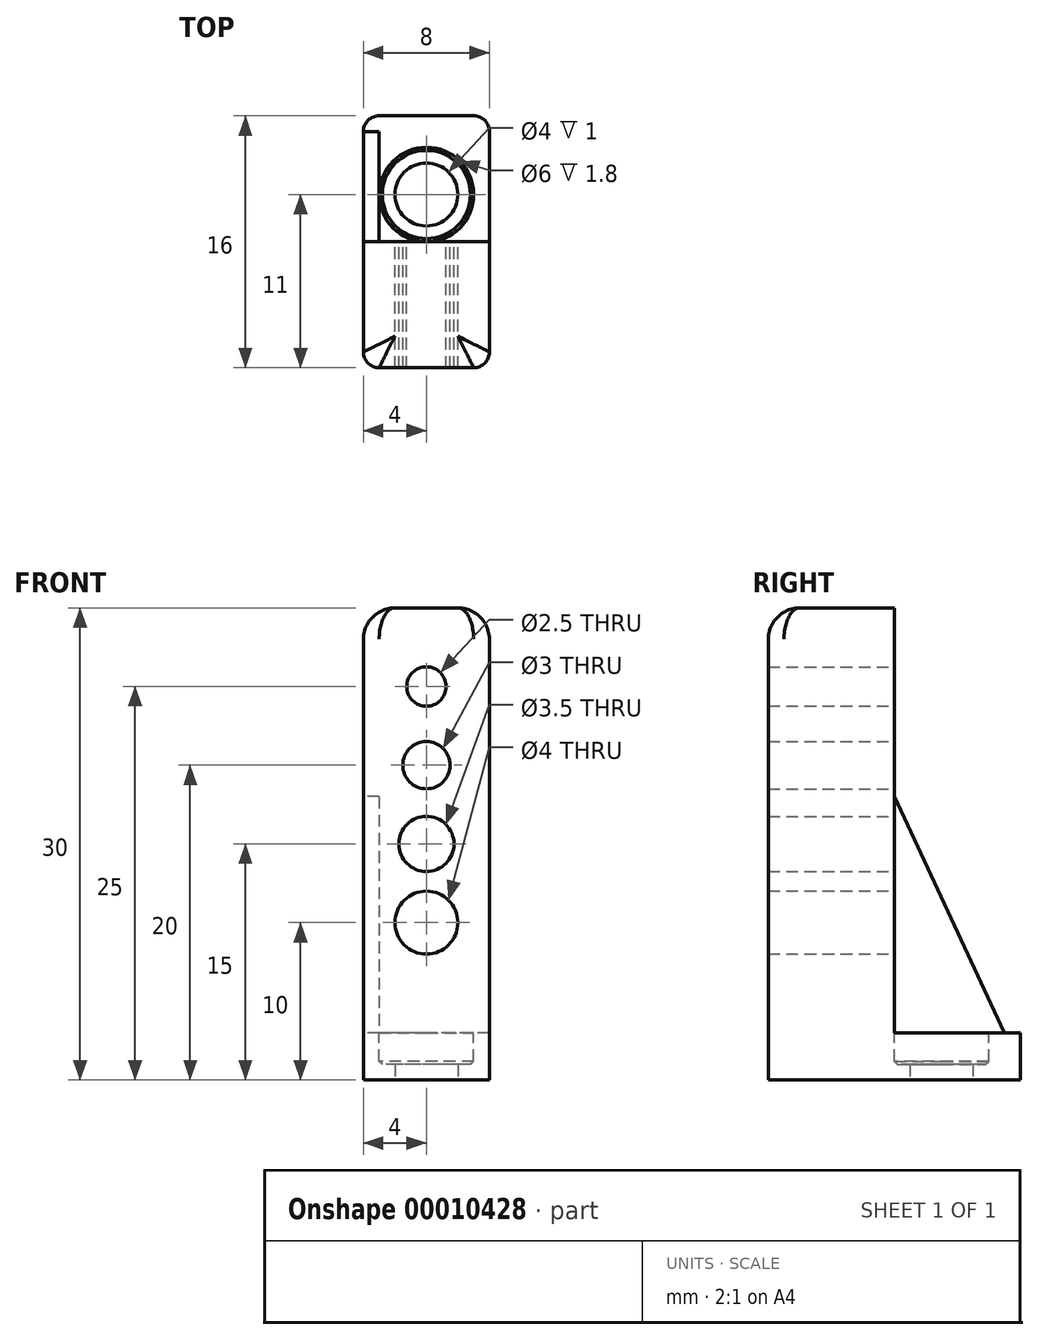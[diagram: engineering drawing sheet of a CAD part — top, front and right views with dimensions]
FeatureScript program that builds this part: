
annotation { "Feature Type Name" : "Feature", "Feature Type Description" : "" }
export const myFeature = defineFeature(function(context is Context, id is Id, definition is map)
    precondition{}
    {
        {
            var Q0;
            Q0=qCreatedBy(makeId("Top.planeOp"),FACE);
            var sketch = newSketch(context, id + "F0", { "sketchPlane" : qUnion([Q0])});
            skLineSegment(sketch, "E0.bottom", {"start": v(3, 5) * mm, "end": v(-3, 5) * mm});
            skLineSegment(sketch, "E0.top", {"start": v(4, -5) * mm, "end": v(-4, -5) * mm});
            skLineSegment(sketch, "E0.left", {"start": v(4, 4) * mm, "end": v(4, -5) * mm});
            skLineSegment(sketch, "E0.right", {"start": v(-4, 4) * mm, "end": v(-4, -5) * mm});
            skPoint(sketch, "E0.middle", {"position": v(0, 0) * mm});
            skCircle(sketch, "E1", {"center": v(0, 0) * mm, "radius": 2 * mm});
            skPoint(sketch, "E2.visualSharp", {"position": v(-4, 5) * mm});
            skArc(sketch, "E2.filletArc", {"start": v(-3, 5) * mm, "mid": v(-3.7, 4.7) * mm, "end": v(-4, 4) * mm});
            skPoint(sketch, "E3.visualSharp", {"position": v(4, 5) * mm});
            skArc(sketch, "E3.filletArc", {"start": v(4, 4) * mm, "mid": v(3.7, 4.7) * mm, "end": v(3, 5) * mm});
            skSolve(sketch);
        }
        {
            var Q0;
            Q0=makeQuery(id+"F0.imprint","IMPRINT",FACE,{"disambiguationData":[TD([[makeQuery(id+"F0.imprint","IMPRINT",EDGE,{"derivedFrom":sQuery(id+"F0.wireOp",EDGE,"E0.bottom")}),1.0]])]});
            extrude(context, id + "F1", {"entities" : qUnion([Q0]), "depth" : 3 * mm});
        }
        {
            var Q0;
            Q0=qCreatedBy(makeId("Top.planeOp"),FACE);
            var sketch = newSketch(context, id + "F2", { "sketchPlane" : qUnion([Q0])});
            skLineSegment(sketch, "E4.top", {"start": v(-4, -3) * mm, "end": v(4, -3) * mm});
            skLineSegment(sketch, "E4.left", {"start": v(-4, -10) * mm, "end": v(-4, -3) * mm});
            skLineSegment(sketch, "E4.right", {"start": v(4, -10) * mm, "end": v(4, -3) * mm});
            skLineSegment(sketch, "E5", {"start": v(-3, -11) * mm, "end": v(3, -11) * mm});
            skPoint(sketch, "E6.visualSharp", {"position": v(-4, -11) * mm});
            skArc(sketch, "E6.filletArc", {"start": v(-4, -10) * mm, "mid": v(-3.7, -10.7) * mm, "end": v(-3, -11) * mm});
            skPoint(sketch, "E7.visualSharp", {"position": v(4, -11) * mm});
            skArc(sketch, "E7.filletArc", {"start": v(3, -11) * mm, "mid": v(3.7, -10.7) * mm, "end": v(4, -10) * mm});
            skSolve(sketch);
        }
        {
            var Q0;
            Q0=qSketchRegion(id+"F2",true);
            extrude(context, id + "F3", {"entities" : qUnion([Q0]), "operationType" : NewBodyOperationType.ADD, "depth" : 30 * mm});
        }
        {
            var Q0;
            Q0=makeQuery(id+"F3.boolean.opBoolean","MERGE",FACE,{"derivedFrom":[makeQuery(id+"F1.opExtrude","SWEPT_FACE",FACE,{"disambiguationData":[OSD([sQuery(id+"F0.wireOp",EDGE,"E0.right")])]}),makeQuery(id+"F3.opExtrude","SWEPT_FACE",FACE,{"disambiguationData":[OSD([sQuery(id+"F2.wireOp",EDGE,"E4.left")])]})]});
            var sketch = newSketch(context, id + "F4", { "sketchPlane" : qUnion([Q0])});
            skLineSegment(sketch, "E8", {"start": v(-4, 3) * mm, "end": v(3, 18) * mm});
            skLineSegment(sketch, "E9", {"start": v(3, 18) * mm, "end": v(3, 3) * mm});
            skLineSegment(sketch, "E10", {"start": v(3, 3) * mm, "end": v(-4, 3) * mm});
            skSolve(sketch);
        }
        {
            var Q0;
            Q0=qSketchRegion(id+"F4",true);
            extrude(context, id + "F5", {"entities" : qUnion([Q0]), "operationType" : NewBodyOperationType.ADD, "oppositeDirection" : true, "depth" : 1 * mm});
        }
        {
            var Q0;
            Q0=makeQuery(id+"F3.opExtrude","SWEPT_FACE",FACE,{"disambiguationData":[OSD([sQuery(id+"F2.wireOp",EDGE,"E4.top")])]});
            var sketch = newSketch(context, id + "F6", { "sketchPlane" : qUnion([Q0])});
            skCircle(sketch, "E11", {"center": v(0, 10) * mm, "radius": 2 * mm});
            skCircle(sketch, "E12", {"center": v(0, 15) * mm, "radius": 1.75 * mm});
            skCircle(sketch, "E13", {"center": v(0, 20) * mm, "radius": 1.5 * mm});
            skCircle(sketch, "E14", {"center": v(0, 25) * mm, "radius": 1.25 * mm});
            skSolve(sketch);
        }
        {
            var Q0;
            Q0 = qSketchRegion(id + "F6", true);
            extrude(context, id + "F7", {"entities" : qUnion([Q0]), "operationType" : NewBodyOperationType.REMOVE, "endBound" : BoundingType.THROUGH_ALL, "oppositeDirection" : true, "depth" : 25 * mm});
        }
        {
            var Q0;
            Q0=makeQuery(id+"F3.opExtrude","CAP_EDGE",EDGE,{"disambiguationData":[OSD([sQuery(id+"F2.wireOp",EDGE,"E4.left")])],"isStart":false});
            var Q1;
            Q1=makeQuery(id+"F3.opExtrude","CAP_EDGE",EDGE,{"disambiguationData":[OSD([sQuery(id+"F2.wireOp",EDGE,"E4.right")])],"isStart":false});
            var Q2;
            Q2=makeQuery(id+"F3.opExtrude","CAP_EDGE",EDGE,{"disambiguationData":[OSD([sQuery(id+"F2.wireOp",EDGE,"E6.filletArc")])],"isStart":false});
            fillet(context, id + "F8", {"entities" : qUnion([Q0, Q1, Q2]), "radius" : 2 * mm, "tangentPropagation" : true, "allowEdgeOverflow" : false});
        }
        {
            var Q0;
            Q0=makeQuery(id+"F1.opExtrude","CAP_FACE",FACE,{"disambiguationData":[OSD([sQuery(id+"F0.wireOp",EDGE,"E0.bottom"),sQuery(id+"F0.wireOp",EDGE,"E0.top"),sQuery(id+"F0.wireOp",EDGE,"E0.left"),sQuery(id+"F0.wireOp",EDGE,"E0.right"),sQuery(id+"F0.wireOp",EDGE,"E1"),sQuery(id+"F0.wireOp",EDGE,"E2.filletArc"),sQuery(id+"F0.wireOp",EDGE,"E3.filletArc")])],"isStart":false});
            var sketch = newSketch(context, id + "F9", { "sketchPlane" : qUnion([Q0])});
            skCircle(sketch, "E15", {"center": v(0, 0) * mm, "radius": 3 * mm});
            skSolve(sketch);
        }
        {
            var Q0;
            Q0 = qSketchRegion(id + "F9", true);
            extrude(context, id + "F10", {"entities" : qUnion([Q0]), "operationType" : NewBodyOperationType.REMOVE, "oppositeDirection" : true, "depth" : 2 * mm});
        }
        {
            var Q0;
            Q0=makeQuery(id+"F10.boolean.opBoolean","COPY",EDGE,{"derivedFrom":makeQuery(id+"F10.opExtrude","CAP_EDGE",EDGE,{"disambiguationData":[OSD([sQuery(id+"F9.wireOp",EDGE,"E15")])],"isStart":false})});
            chamfer(context, id + "F11", {"entities" : qUnion([Q0]), "width" : .2 * mm, "tangentPropagation" : true});
        }
    });
